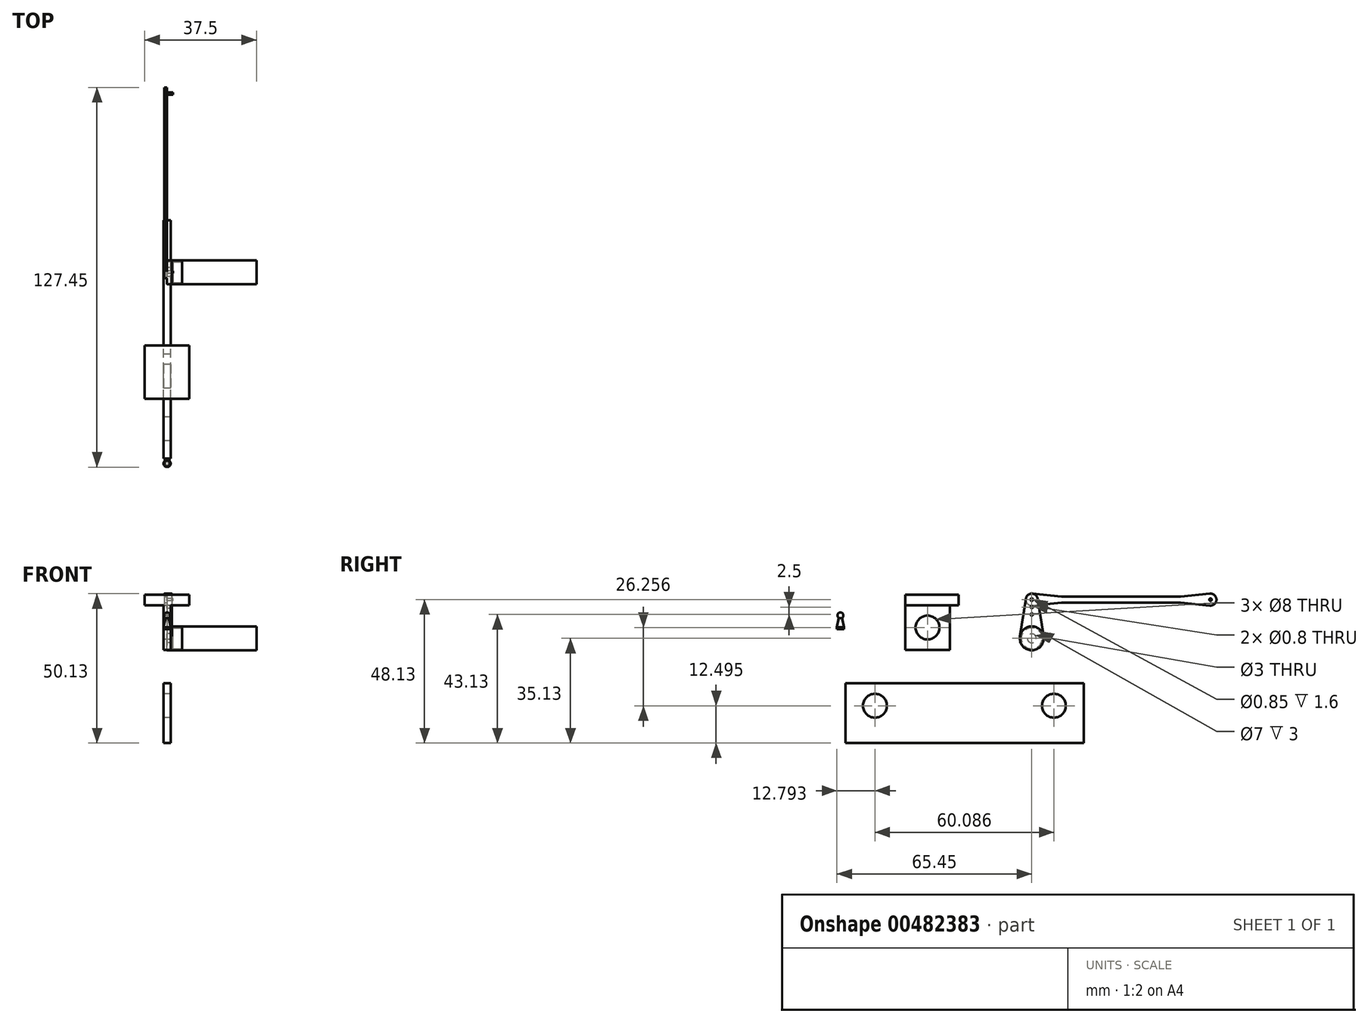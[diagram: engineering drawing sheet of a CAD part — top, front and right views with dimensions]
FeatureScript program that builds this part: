
annotation { "Feature Type Name" : "Feature", "Feature Type Description" : "" }
export const myFeature = defineFeature(function(context is Context, id is Id, definition is map)
    precondition{}
    {
        {
            var Q0;
            Q0=qCreatedBy(makeId("Right.planeOp"),FACE);
            var sketch = newSketch(context, id + "F0", { "sketchPlane" : qUnion([Q0])});
            skCircle(sketch, "E0", {"center": v(0, 0) * mm, "radius": 4 * mm});
            skCircle(sketch, "E1", {"center": v(0, 13) * mm, "radius": 2 * mm});
            skLineSegment(sketch, "E2", {"start": v(-1.98, 13.3) * mm, "end": v(-3.95, 0.62) * mm});
            skLineSegment(sketch, "E3", {"start": v(1.98, 13.3) * mm, "end": v(3.95, 0.62) * mm});
            skLineSegment(sketch, "E4", {"start": v(0, 13) * mm, "end": v(0, 0) * mm, "construction": true});
            skCircle(sketch, "E5", {"center": v(0, 0) * mm, "radius": 1.5 * mm});
            skCircle(sketch, "E6", {"center": v(0, 13) * mm, "radius": 0.42 * mm});
            skCircle(sketch, "E7.0.1.0", {"center": v(0, 10.5) * mm, "radius": 0.4 * mm});
            skLineSegment(sketch, "E7.direction2", {"start": v(0, 13) * mm, "end": v(0, 10.5) * mm, "construction": true});
            skCircle(sketch, "E8.0.1.0", {"center": v(0, 8) * mm, "radius": 0.4 * mm});
            skLineSegment(sketch, "E9", {"start": v(0, 10.5) * mm, "end": v(0, 8) * mm, "construction": true});
            skLineSegment(sketch, "E10", {"start": v(-17.13, 13) * mm, "end": v(24.81, 13) * mm, "construction": true});
            skLineSegment(sketch, "E11", {"start": v(-6.17, 15) * mm, "end": v(18.5, 15) * mm, "construction": true});
            skLineSegment(sketch, "E12", {"start": v(-6.02, 11) * mm, "end": v(18.13, 11) * mm, "construction": true});
            skLineSegment(sketch, "E13", {"start": v(14.47, 16) * mm, "end": v(14.47, 9.33) * mm, "construction": true});
            skCircle(sketch, "E14", {"center": v(9.9, 13) * mm, "radius": 1 * mm});
            skLineSegment(sketch, "E15", {"start": v(0.2, 14.99) * mm, "end": v(10, 14) * mm});
            skLineSegment(sketch, "E16", {"start": v(10, 12) * mm, "end": v(0, 10.99) * mm});
            skCircle(sketch, "E17", {"center": v(0, 13) * mm, "radius": 0.4 * mm});
            skLineSegment(sketch, "E18", {"start": v(10, 14) * mm, "end": v(30, 14) * mm});
            skLineSegment(sketch, "E19.MirrorCS", {"start": v(10, 12) * mm, "end": v(30, 12) * mm});
            skLineSegment(sketch, "E20", {"start": v(30, 14) * mm, "end": v(30, 12) * mm});
            skCircle(sketch, "E21", {"center": v(-35, 3.62) * mm, "radius": 4 * mm});
            skLineSegment(sketch, "E22", {"start": v(-45.57, 1.96) * mm, "end": v(-23.6, 1.96) * mm, "construction": true});
            skLineSegment(sketch, "E23", {"start": v(-35, 12.95) * mm, "end": v(-35, -6.89) * mm, "construction": true});
            skLineSegment(sketch, "E24.bottom", {"start": v(-42.5, 11.12) * mm, "end": v(-27.5, 11.12) * mm});
            skLineSegment(sketch, "E24.top", {"start": v(-42.5, -3.88) * mm, "end": v(-27.5, -3.88) * mm});
            skLineSegment(sketch, "E24.left", {"start": v(-42.5, 11.12) * mm, "end": v(-42.5, -3.88) * mm});
            skLineSegment(sketch, "E24.right", {"start": v(-27.5, 11.12) * mm, "end": v(-27.5, -3.88) * mm});
            skLineSegment(sketch, "E25.bottom", {"start": v(-42.5, 11.12) * mm, "end": v(-24.56, 11.12) * mm});
            skLineSegment(sketch, "E25.top", {"start": v(-42.5, 14.64) * mm, "end": v(-24.56, 14.64) * mm});
            skLineSegment(sketch, "E25.left", {"start": v(-42.5, 11.12) * mm, "end": v(-42.5, 14.64) * mm});
            skLineSegment(sketch, "E25.right", {"start": v(-24.56, 11.12) * mm, "end": v(-24.56, 14.64) * mm});
            skLineSegment(sketch, "E26", {"start": v(10, 14) * mm, "end": v(10, 23.15) * mm, "construction": true});
            skLineSegment(sketch, "E27", {"start": v(0, 13) * mm, "end": v(0, 25.95) * mm, "construction": true});
            skLineSegment(sketch, "E28", {"start": v(0, 22.2) * mm, "end": v(10, 22.2) * mm, "construction": true});
            skLineSegment(sketch, "E29.bottom", {"start": v(-62.57, -15.13) * mm, "end": v(17.43, -15.13) * mm});
            skLineSegment(sketch, "E29.top", {"start": v(-62.57, -35.13) * mm, "end": v(17.43, -35.13) * mm});
            skLineSegment(sketch, "E29.left", {"start": v(-62.57, -15.13) * mm, "end": v(-62.57, -35.13) * mm});
            skLineSegment(sketch, "E29.right", {"start": v(17.43, -15.13) * mm, "end": v(17.43, -35.13) * mm});
            skLineSegment(sketch, "E30.0", {"start": v(30.61, -22.63) * mm, "end": v(-81.37, -22.63) * mm, "construction": true});
            skPoint(sketch, "E31.endSnap0", {"position": v(17.43, -25.13) * mm});
            skLineSegment(sketch, "E32.0", {"start": v(-52.66, -4.93) * mm, "end": v(-52.66, -43.48) * mm, "construction": true});
            skLineSegment(sketch, "E33.0", {"start": v(7.43, -6.2) * mm, "end": v(7.43, -43.48) * mm, "construction": true});
            skCircle(sketch, "E34", {"center": v(-52.66, -22.63) * mm, "radius": 4 * mm});
            skCircle(sketch, "E35", {"center": v(7.43, -22.63) * mm, "radius": 4 * mm});
            skLineSegment(sketch, "E36", {"start": v(-64.25, 10) * mm, "end": v(-64.25, -2.92) * mm, "construction": true});
            skLineSegment(sketch, "E37", {"start": v(-68.41, 7.67) * mm, "end": v(-59.37, 7.67) * mm, "construction": true});
            skCircle(sketch, "E38", {"center": v(-64.25, 7.67) * mm, "radius": 1 * mm});
            skLineSegment(sketch, "E39", {"start": v(-67.7, 7.67) * mm, "end": v(-67.7, 3.67) * mm, "construction": true});
            skLineSegment(sketch, "E40.bottom", {"start": v(-64.77, 6.82) * mm, "end": v(-63.72, 6.82) * mm, "construction": true});
            skLineSegment(sketch, "E40.left", {"start": v(-64.77, 6.82) * mm, "end": v(-64.77, 3.18) * mm, "construction": true});
            skLineSegment(sketch, "E40.right", {"start": v(-63.72, 6.82) * mm, "end": v(-63.72, 3.18) * mm, "construction": true});
            skPoint(sketch, "E40.middle", {"position": v(-64.25, 5) * mm});
            skLineSegment(sketch, "E41", {"start": v(-67.7, 3.67) * mm, "end": v(-61.56, 3.67) * mm, "construction": true});
            skLineSegment(sketch, "E42", {"start": v(-64.77, 6.82) * mm, "end": v(-65.45, 3.67) * mm});
            skLineSegment(sketch, "E43", {"start": v(-65.45, 3.67) * mm, "end": v(-65.45, 3.14) * mm});
            skLineSegment(sketch, "E44", {"start": v(-65.45, 3.14) * mm, "end": v(-64.25, 3.14) * mm});
            skLineSegment(sketch, "E45.MirrorCS", {"start": v(-63.72, 6.82) * mm, "end": v(-63.05, 3.67) * mm});
            skLineSegment(sketch, "E46.MirrorCS", {"start": v(-63.05, 3.67) * mm, "end": v(-63.05, 3.14) * mm});
            skLineSegment(sketch, "E47.MirrorCS", {"start": v(-63.05, 3.14) * mm, "end": v(-64.25, 3.14) * mm});
            skLineSegment(sketch, "E48", {"start": v(-64.25, 8.67) * mm, "end": v(-64.25, 3.14) * mm});
            skCircle(sketch, "E49", {"center": v(50.94, 0) * mm, "radius": 4 * mm});
            skCircle(sketch, "E50", {"center": v(50.94, 13) * mm, "radius": 2 * mm});
            skLineSegment(sketch, "E51", {"start": v(48.96, 13.3) * mm, "end": v(46.99, 0.62) * mm});
            skLineSegment(sketch, "E52", {"start": v(52.92, 13.3) * mm, "end": v(54.9, 0.62) * mm});
            skLineSegment(sketch, "E53", {"start": v(50.94, 13) * mm, "end": v(50.94, 0) * mm, "construction": true});
            skCircle(sketch, "E54", {"center": v(50.94, 0) * mm, "radius": 1.5 * mm});
            skCircle(sketch, "E55", {"center": v(50.94, 13) * mm, "radius": 0.42 * mm});
            skCircle(sketch, "E56.0.1.0", {"center": v(50.94, 10.5) * mm, "radius": 0.4 * mm});
            skLineSegment(sketch, "E56.direction2", {"start": v(50.94, 13) * mm, "end": v(50.94, 10.5) * mm, "construction": true});
            skCircle(sketch, "E57.0.1.0", {"center": v(50.94, 8) * mm, "radius": 0.4 * mm});
            skLineSegment(sketch, "E58", {"start": v(50.94, 10.5) * mm, "end": v(50.94, 8) * mm, "construction": true});
            skCircle(sketch, "E59", {"center": v(50.94, 13) * mm, "radius": 0.4 * mm});
            skSolve(sketch);
        }
        {
            var Q0;
            {var subQ0=sQuery(id+"F0.wireOp",EDGE,"E2");Q0=makeQuery(id+"F0.imprint","IMPRINT",FACE,{"disambiguationData":[TD([[makeQuery(id+"F0.imprint","IMPRINT",EDGE,{"derivedFrom":subQ0}),1.0]])]});}
            var Q1;
            {var subQ0=sQuery(id+"F0.wireOp",EDGE,"E1");var subQ1=makeQuery(id+"F0.imprint","INTERSECT",VERTEX,{"derivedFrom":[subQ0,sQuery(id+"F0.wireOp",EDGE,"E2")]});Q1=makeQuery(id+"F0.imprint","IMPRINT",FACE,{"disambiguationData":[TD([[makeQuery(id+"F0.imprint","IMPRINT",EDGE,{"disambiguationData":[TD([[subQ1,1.0]])],"derivedFrom":subQ0}),1.0]])]});}
            var Q2;
            {var subQ0=sQuery(id+"F0.wireOp",EDGE,"E3");var subQ1=sQuery(id+"F0.wireOp",EDGE,"E1");var subQ2=makeQuery(id+"F0.imprint","INTERSECT",VERTEX,{"derivedFrom":[subQ1,subQ0]});Q2=makeQuery(id+"F0.imprint","IMPRINT",FACE,{"disambiguationData":[TD([[makeQuery(id+"F0.imprint","IMPRINT",EDGE,{"disambiguationData":[TD([[subQ2,1.0]])],"derivedFrom":subQ1}),-1.0]])]});}
            extrude(context, id + "F1", {"entities" : qUnion([Q0, Q1, Q2]), "depth" : 1.6 * mm});
        }
        {
            var Q0;
            Q0=makeQuery(id+"F0.imprint","IMPRINT",FACE,{"disambiguationData":[TD([[makeQuery(id+"F0.imprint","IMPRINT",EDGE,{"derivedFrom":sQuery(id+"F0.wireOp",EDGE,"E5")}),-1.0]])]});
            extrude(context, id + "F2", {"entities" : qUnion([Q0]), "operationType" : NewBodyOperationType.ADD, "depth" : 5 * mm});
        }
        {
            var Q0;
            Q0=makeQuery(id+"F2.opExtrude","CAP_FACE",FACE,{"disambiguationData":[OSD([sQuery(id+"F0.wireOp",EDGE,"E0"),sQuery(id+"F0.wireOp",EDGE,"E5")])],"isStart":false});
            var sketch = newSketch(context, id + "F3", { "sketchPlane" : qUnion([Q0])});
            skCircle(sketch, "E60", {"center": v(0, 0) * mm, "radius": 3.5 * mm});
            skSolve(sketch);
        }
        {
            var Q0;
            Q0=makeQuery(id+"F3.imprint","IMPRINT",FACE,{"disambiguationData":[TD([[makeQuery(id+"F3.imprint","IMPRINT",EDGE,{"derivedFrom":sQuery(id+"F3.wireOp",EDGE,"E60")}),1.0]])]});
            extrude(context, id + "F4", {"entities" : qUnion([Q0]), "operationType" : NewBodyOperationType.REMOVE, "oppositeDirection" : true, "depth" : 3 * mm});
        }
        {
            var Q0;
            {var subQ0=sQuery(id+"F0.wireOp",EDGE,"E15");Q0=makeQuery(id+"F0.imprint","IMPRINT",FACE,{"disambiguationData":[TD([[makeQuery(id+"F0.imprint","IMPRINT",EDGE,{"derivedFrom":subQ0}),-1.0]])]});}
            var Q1;
            Q1=makeQuery(id+"F0.imprint","IMPRINT",FACE,{"disambiguationData":[TD([[makeQuery(id+"F0.imprint","IMPRINT",EDGE,{"derivedFrom":sQuery(id+"F0.wireOp",EDGE,"E6")}),-1.0]])]});
            var Q2;
            {var subQ0=sQuery(id+"F0.wireOp",EDGE,"E3");var subQ1=sQuery(id+"F0.wireOp",EDGE,"E1");var subQ2=makeQuery(id+"F0.imprint","INTERSECT",VERTEX,{"derivedFrom":[subQ1,subQ0]});Q2=makeQuery(id+"F0.imprint","IMPRINT",FACE,{"disambiguationData":[TD([[makeQuery(id+"F0.imprint","IMPRINT",EDGE,{"disambiguationData":[TD([[subQ2,1.0]])],"derivedFrom":subQ1}),-1.0]])]});}
            var Q3;
            Q3=makeQuery(id+"F0.imprint","IMPRINT",FACE,{"disambiguationData":[TD([[makeQuery(id+"F0.imprint","IMPRINT",EDGE,{"derivedFrom":sQuery(id+"F0.wireOp",EDGE,"E17")}),1.0]])]});
            var Q4;
            Q4=makeQuery(id+"F0.imprint","IMPRINT",FACE,{"disambiguationData":[TD([[makeQuery(id+"F0.imprint","IMPRINT",EDGE,{"derivedFrom":sQuery(id+"F0.wireOp",EDGE,"E6")}),1.0]])]});
            var Q5;
            {var subQ0=sQuery(id+"F0.wireOp",EDGE,"E18");Q5=makeQuery(id+"F0.imprint","IMPRINT",FACE,{"disambiguationData":[TD([[makeQuery(id+"F0.imprint","IMPRINT",EDGE,{"derivedFrom":subQ0}),-1.0]])]});}
            var Q6;
            {var subQ0=sQuery(id+"F0.wireOp",EDGE,"E14");var subQ1=makeQuery(id+"F0.imprint","INTERSECT",VERTEX,{"derivedFrom":[subQ0,sQuery(id+"F0.wireOp",EDGE,"E15"),sQuery(id+"F0.wireOp",EDGE,"E18")]});Q6=makeQuery(id+"F0.imprint","IMPRINT",FACE,{"disambiguationData":[TD([[makeQuery(id+"F0.imprint","IMPRINT",EDGE,{"disambiguationData":[TD([[subQ1,-1.0]])],"derivedFrom":subQ0}),1.0]])]});}
            extrude(context, id + "F5", {"entities" : qUnion([Q0, Q1, Q2, Q3, Q4, Q5, Q6]), "oppositeDirection" : true, "depth" : 1 * mm});
        }
        {
            var Q0;
            Q0=makeQuery(id+"F0.imprint","IMPRINT",FACE,{"disambiguationData":[TD([[makeQuery(id+"F0.imprint","IMPRINT",EDGE,{"derivedFrom":sQuery(id+"F0.wireOp",EDGE,"E17")}),1.0]])]});
            extrude(context, id + "F6", {"entities" : qUnion([Q0]), "operationType" : NewBodyOperationType.ADD, "depth" : 2 * mm});
        }
        {
            var Q0;
            Q0=makeQuery(id+"F5.opExtrude","SWEPT_BODY",BODY,{"disambiguationData":[OSD([sQuery(id+"F0.wireOp",EDGE,"E1"),sQuery(id+"F0.wireOp",EDGE,"E15"),sQuery(id+"F0.wireOp",EDGE,"E16"),sQuery(id+"F0.wireOp",EDGE,"E18"),sQuery(id+"F0.wireOp",EDGE,"E19.MirrorCS"),sQuery(id+"F0.wireOp",EDGE,"E20")])]});
            var Q1;
            Q1=makeQuery(id+"F5.opExtrude","SWEPT_FACE",FACE,{"disambiguationData":[OSD([sQuery(id+"F0.wireOp",EDGE,"E20")])]});
            mirror(context, id + "F7", {"operationType" : NewBodyOperationType.ADD, "entities" : qUnion([Q0]), "mirrorPlane" : qUnion([Q1])});
        }
        {
            var Q0;
            Q0=makeQuery(id+"F0.imprint","IMPRINT",FACE,{"disambiguationData":[TD([[makeQuery(id+"F0.imprint","IMPRINT",EDGE,{"derivedFrom":sQuery(id+"F0.wireOp",EDGE,"E5")}),-1.0]])]});
            var Q1;
            Q1=makeQuery(id+"F0.imprint","IMPRINT",FACE,{"disambiguationData":[TD([[makeQuery(id+"F0.imprint","IMPRINT",EDGE,{"derivedFrom":sQuery(id+"F0.wireOp",EDGE,"E5")}),1.0]])]});
            extrude(context, id + "F8", {"entities" : qUnion([Q0, Q1]), "depth" : 30 * mm});
        }
        {
            var Q0;
            Q0=makeQuery(id+"F1.opExtrude","SWEPT_BODY",BODY,{"disambiguationData":[OSD([sQuery(id+"F0.wireOp",EDGE,"E0"),sQuery(id+"F0.wireOp",EDGE,"E1"),sQuery(id+"F0.wireOp",EDGE,"E2"),sQuery(id+"F0.wireOp",EDGE,"E3"),sQuery(id+"F0.wireOp",EDGE,"E6"),sQuery(id+"F0.wireOp",EDGE,"E7.0.1.0"),sQuery(id+"F0.wireOp",EDGE,"E8.0.1.0")])]});
            var Q1;
            Q1=makeQuery(id+"F8.opExtrude","SWEPT_BODY",BODY,{"disambiguationData":[OSD([sQuery(id+"F0.wireOp",EDGE,"E0")])]});
            booleanBodies(context, id + "F9", {"operationType" : BooleanOperationType.SUBTRACTION, "tools" : qUnion([Q0]), "targets" : qUnion([Q1]), "keepTools" : true});
        }
        {
            var Q0;
            Q0=makeQuery(id+"F0.imprint","IMPRINT",FACE,{"disambiguationData":[TD([[makeQuery(id+"F0.imprint","IMPRINT",EDGE,{"derivedFrom":sQuery(id+"F0.wireOp",EDGE,"E21")}),-1.0]])]});
            extrude(context, id + "F10", {"entities" : qUnion([Q0]), "endBound" : BoundingType.SYMMETRIC, "depth" : 2.5 * mm});
        }
        {
            var Q0;
            Q0=makeQuery(id+"F0.imprint","IMPRINT",FACE,{"disambiguationData":[TD([[makeQuery(id+"F0.imprint","IMPRINT",EDGE,{"derivedFrom":sQuery(id+"F0.wireOp",EDGE,"E25.top")}),-1.0]])]});
            extrude(context, id + "F11", {"entities" : qUnion([Q0]), "operationType" : NewBodyOperationType.ADD, "endBound" : BoundingType.SYMMETRIC, "depth" : 15 * mm});
        }
        {
            var Q0;
            Q0=makeQuery(id+"F0.imprint","IMPRINT",FACE,{"disambiguationData":[TD([[makeQuery(id+"F0.imprint","IMPRINT",EDGE,{"derivedFrom":sQuery(id+"F0.wireOp",EDGE,"E29.bottom")}),-1.0]])]});
            extrude(context, id + "F12", {"entities" : qUnion([Q0]), "endBound" : BoundingType.SYMMETRIC, "depth" : 2.5 * mm});
        }
        {
            var Q0;
            {var subQ0=sQuery(id+"F0.wireOp",EDGE,"E38");var subQ1=makeQuery(id+"F0.imprint","INTERSECT",VERTEX,{"derivedFrom":[subQ0,sQuery(id+"F0.wireOp",EDGE,"E42")]});Q0=makeQuery(id+"F0.imprint","IMPRINT",FACE,{"disambiguationData":[TD([[makeQuery(id+"F0.imprint","IMPRINT",EDGE,{"disambiguationData":[TD([[subQ1,1.0]])],"derivedFrom":subQ0}),1.0]])]});}
            var Q1;
            {var subQ0=sQuery(id+"F0.wireOp",EDGE,"E42");Q1=makeQuery(id+"F0.imprint","IMPRINT",FACE,{"disambiguationData":[TD([[makeQuery(id+"F0.imprint","IMPRINT",EDGE,{"derivedFrom":subQ0}),1.0]])]});}
            var Q2;
            Q2=sQuery(id+"F0.wireOp",EDGE,"E36");
            revolve(context, id + "F13", {"entities" : qUnion([Q0, Q1]), "axis" : qUnion([Q2]), "revolveType" : RevolveType.FULL});
        }
    });
